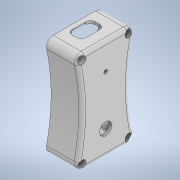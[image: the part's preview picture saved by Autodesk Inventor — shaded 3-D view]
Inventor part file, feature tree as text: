
AUTODESK INVENTOR PART (.ipt)
format: ipt  version: 2021 (Build 250183000, 183)  size: 609,792 bytes
history: native  units: mm
features: extrude x10, sketch x10, fillet x5, projected_geometry x4, mirror x2, shell x1, plane x1
ambient origin geometry x8: Origin, YZ Plane, XZ Plane, XY Plane, X Axis, Y Axis, Z Axis, Center Point
bodies: Solid1 (feature_tree)
feature tree (33):
  extrude  "Extrusion1"  Depth=27.0mm
  extrude  "Extrusion5"  Depth=2.0mm
  fillet  "Fillet1"  Radius=1.5mm
  shell  "Shell1"  Thickness=3.8mm
  extrude  "Extrusion6"  Depth=4.0mm
  extrude  "Extrusion7"  Depth=2.4mm
  fillet  "Fillet3"  Radius=17.78mm
  extrude  "Extrusion8"  Depth=6.8mm TaperAngle=0.0deg
  extrude  "Extrusion14"  Depth=11.4mm
  extrude  "Extrusion15"  Depth=13.5mm
  fillet  "Fillet8"  Radius=1.5mm
  extrude  "Extrusion16"  Depth=39.37mm
  fillet  "Fillet9"  Radius=7.1mm
  mirror  "Mirror5"
  plane  "Work Plane5"
  mirror  "Mirror8"
  extrude  "Extrusion17"  Depth=10.795mm
  extrude  "Extrusion18"  Depth=0.25mm
  fillet  "Fillet11"  Radius=5.5mm
  sketch  "Sketch1"  dims[d0=18.0mm d1=27.0mm]
  sketch  "Sketch5"  dims[d2=58.0mm d3=0.0mm d4=2.0mm d5=1.5mm d26=3.8mm]
  sketch  "Sketch6"  dims[d27=0.0mm d28=0.0mm d29=4.0mm]
  sketch  "Sketch7"  dims[d33=5.0mm d34=2.4mm d36=17.78mm]
  sketch  "Sketch8"  dims[d37=45.72mm d38=6.8mm d39=0.0mm]
  sketch  "Sketch18"  dims[d40=3.0mm d41=11.4mm]
  sketch  "Sketch19"  dims[d42=8.2mm d43=13.5mm d44=1.5mm d45=0.0mm]
  sketch  "Sketch20"  dims[d46=3.0mm d47=39.37mm d48=7.1mm]
  sketch  "Sketch21"  dims[d49=2.0mm d50=10.795mm]
  sketch  "Sketch22"  dims[d51=0.0mm d52=0.0mm d94=1.9mm d95=5.5mm d96=10.0mm d97=0.0mm d98=4.0mm d100=10.0mm d101=0.0mm d102=0.5mm d103=3.75mm d104=6.8mm d105=0.0mm d106=0.25mm d107=1.5mm d108=2.1mm d109=0.0mm d110=0.0mm d111=3.0mm d112=0.0mm d114=4.0mm d115=0.75mm d116=0.25mm]
  projected_geometry  "Project Cut Edges6"
  projected_geometry  "Project Cut Edges10"
  projected_geometry  "Project Cut Edges11"
  projected_geometry  "Project Cut Edges12"
